# Revit family: Altea 300 LED
name_source: partatom
category: Lighting Fixtures
revit_build: Autodesk Revit 2018 (Build: 20170223_1515(x64)
units: mm (PartAtom-declared; Revit-internal decimal feet)

## family parameters
Always vertical = Yes
Cut with Voids When Loaded = No
Host = Ceiling
Light Source = Yes
OmniClass Number = 23.80.70.11
OmniClass Title = Luminaries for Internal Lighting
Part Type = Normal
Room Calculation Point = No
Round Connector Dimension = Use Diameter
Shared = No

## types (2) — shared parameters
Color Filter = 16777215
Dimming Lamp Color Temperature Shift = <None>

## per-type parameters (varying)
| type | Dimmable | Driver Included | Driver Required | Electrical Class | Main Finish | Main Material | Photometric Web File | Product Name | Tilt Angle |
| CE | N | Y | Y | 2 | Various | Various | TRN-18319  Altea 300 LED 8047 .ies | Altea 300 | 90.00° |
| ETL |  |  |  |  |  |  | generic |  | 60.00° |

## geometry (parser evidence)
native form markers: Sweep x1
no freeform markers — native parametric forms only
